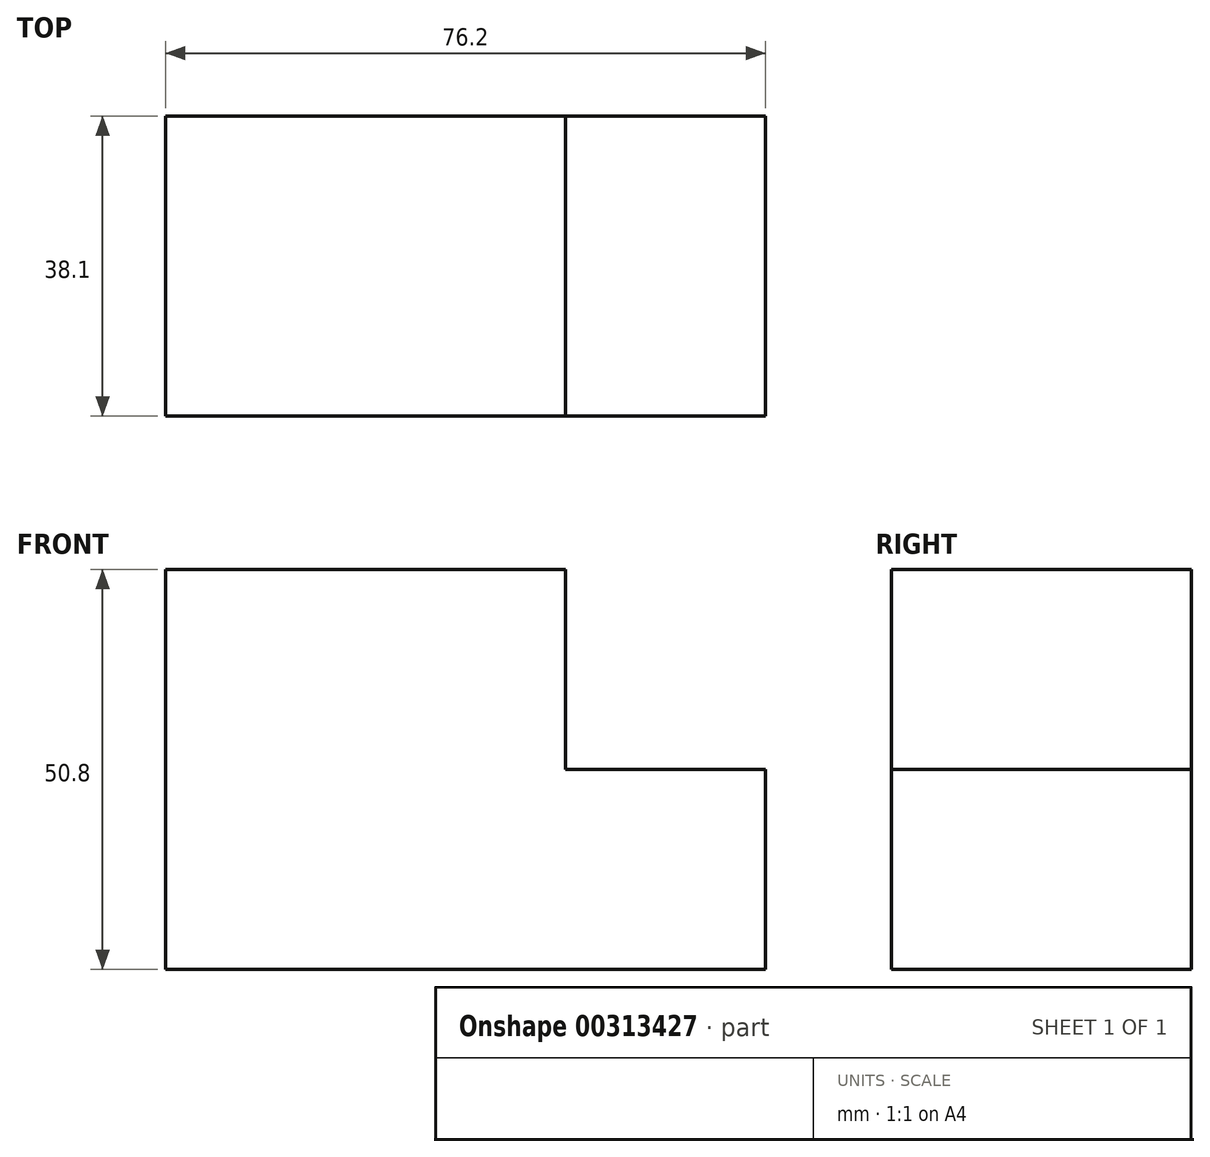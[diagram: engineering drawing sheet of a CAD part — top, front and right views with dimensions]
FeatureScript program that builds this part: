
annotation { "Feature Type Name" : "Feature", "Feature Type Description" : "" }
export const myFeature = defineFeature(function(context is Context, id is Id, definition is map)
    precondition{}
    {
        {
            var Q0;
            Q0=qCreatedBy(makeId("Front.planeOp"),FACE);
            var sketch = newSketch(context, id + "F0", { "sketchPlane" : qUnion([Q0])});
            skLineSegment(sketch, "E0", {"start": v(-49.63, -19.54) * mm, "end": v(26.57, -19.54) * mm});
            skLineSegment(sketch, "E1", {"start": v(26.57, -19.54) * mm, "end": v(26.57, 5.86) * mm});
            skLineSegment(sketch, "E2", {"start": v(26.57, 5.86) * mm, "end": v(1.17, 5.86) * mm});
            skLineSegment(sketch, "E3", {"start": v(1.17, 5.86) * mm, "end": v(1.17, 31.26) * mm});
            skLineSegment(sketch, "E4", {"start": v(1.17, 31.26) * mm, "end": v(-49.63, 31.26) * mm});
            skLineSegment(sketch, "E5", {"start": v(-49.63, 31.26) * mm, "end": v(-49.63, -19.54) * mm});
            skSolve(sketch);
        }
        {
            var Q0;
            Q0=makeQuery(id+"F0.imprint","IMPRINT",FACE,{"disambiguationData":[TD([[makeQuery(id+"F0.imprint","IMPRINT",EDGE,{"derivedFrom":sQuery(id+"F0.wireOp",EDGE,"E0")}),1.0]])]});
            extrude(context, id + "F1", {"entities" : qUnion([Q0]), "depth" : 38.1 * mm});
        }
    });
